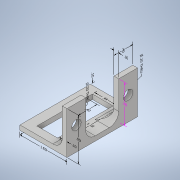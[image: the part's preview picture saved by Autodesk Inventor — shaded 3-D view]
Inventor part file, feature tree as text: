
AUTODESK INVENTOR PART (.ipt)
format: ipt  version: 2020 (Build 240168000, 168)  size: 186,368 bytes
history: native  units: in
note: dims shown in document units (in); Inventor stores cm internally (conversion verified against a paired STEP export)
features: sketch x5, extrude x3, hole x2, other x2, fillet x1
ambient origin geometry x8: Origin, YZ Plane, XZ Plane, XY Plane, X Axis, Y Axis, Z Axis, Center Point
bodies: Solid1 (feature_tree)
feature tree (13):
  extrude  "Extrusion1"  Depth=1.5in
  extrude  "Extrusion2"  Depth=0.2in
  extrude  "Extrusion3"  Depth=0.2in
  hole  "Hole1"  [1 undecoded]
  hole  "Hole2"  [1 undecoded]
  fillet  "Fillet1"  Radius=0.4in
  sketch  "Sketch1"  dims[d0=1.0in d1=1.5in]
  sketch  "Sketch3"  dims[d2=0.1in d3=0.0in d7=0.2in]
  sketch  "Sketch4"  dims[d8=0.16in d9=0.2in]
  sketch  "Sketch5"  dims[d10=0.16in d11=0.44in]
  sketch  "Sketch6"  dims[d12=0.1in d13=0.0in d14=0.1in d15=0.4in d16=0.1in d17=0.4in d18=0.8in d19=0.0in d20=0.4in d21=0.2in d22=0.75in d23=0.375in d24=0.25in d25=0.5635in d26=1.0in d27=0.8108in d28=0.4in d29=0.2in d30=0.75in d31=0.375in d32=0.25in d33=0.5635in d34=1.0in d35=0.8108in d76=0.2in d39=0.3313in d40=0.2404in d41=1.18in d42=0.0291in d43=0.368in d44=0.44in d45=0.1913in d46=0.2744in d47=1.5in d48=0.3605in d49=0.3601in d50=0.1in d51=0.0149in d52=0.1949in d53=1.0in d54=1.3283in d56=1.3744in d58=0.0808in d59=0.0305in d60=0.1in d61=0.2024in d62=0.3795in d63=0.9in d64=0.186in d65=0.2159in d66=0.4in d67=0.1931in d68=0.0746in d69=0.4in d70=0.1349in d71=0.1348in d72=0.8in d73=0.1747in d74=0.1613in d75=0.1in d77=0.2598in d78=0.2257in d79=1.18in d80=0.105in d81=0.3223in d82=0.44in]
  other  "Linear Dimension 12"
  other  "Linear Dimension 13"
note: 2 required parameter values undecoded (feature->parameter linkage not recoverable at this tier; creation-order binding heuristic only, values carry confidence <= 0.55)
